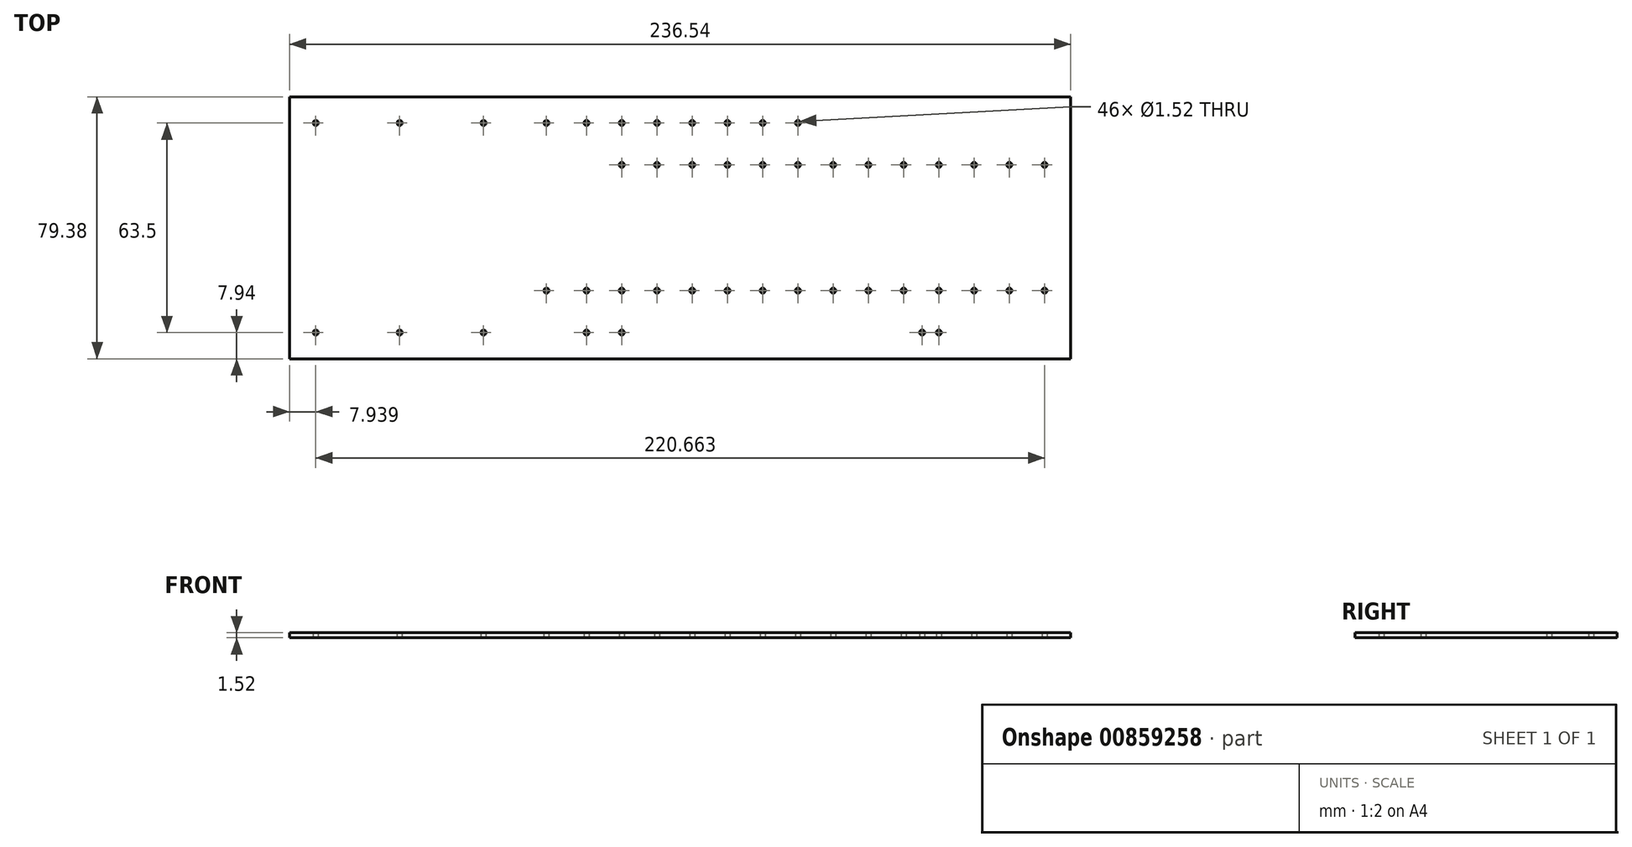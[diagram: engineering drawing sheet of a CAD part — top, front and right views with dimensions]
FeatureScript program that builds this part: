
annotation { "Feature Type Name" : "Feature", "Feature Type Description" : "" }
export const myFeature = defineFeature(function(context is Context, id is Id, definition is map)
    precondition{}
    {
        {
            var Q0;
            Q0=qCreatedBy(makeId("Top.planeOp"),FACE);
            var sketch = newSketch(context, id + "F0", { "sketchPlane" : qUnion([Q0])});
            skLineSegment(sketch, "E0.bottom", {"start": v(118.27, 39.69) * mm, "end": v(-118.27, 39.69) * mm});
            skLineSegment(sketch, "E0.top", {"start": v(118.27, -39.69) * mm, "end": v(-118.27, -39.69) * mm});
            skLineSegment(sketch, "E0.left", {"start": v(118.27, 39.69) * mm, "end": v(118.27, -39.69) * mm});
            skLineSegment(sketch, "E0.right", {"start": v(-118.27, 39.69) * mm, "end": v(-118.27, -39.69) * mm});
            skPoint(sketch, "E0.middle", {"position": v(0, 0) * mm});
            skPoint(sketch, "E1", {"position": v(-110.33, -31.75) * mm});
            skPoint(sketch, "E2", {"position": v(-84.93, -31.75) * mm});
            skPoint(sketch, "E3", {"position": v(-59.53, -31.75) * mm});
            skPoint(sketch, "E4", {"position": v(-59.53, 31.75) * mm});
            skPoint(sketch, "E5", {"position": v(-84.93, 31.75) * mm});
            skPoint(sketch, "E6", {"position": v(-110.33, 31.75) * mm});
            skPoint(sketch, "E7", {"position": v(-40.48, 31.75) * mm});
            skPoint(sketch, "E8", {"position": v(-17.68, 31.75) * mm});
            skPoint(sketch, "E9", {"position": v(-7.02, 31.75) * mm});
            skPoint(sketch, "E10", {"position": v(3.65, 31.75) * mm});
            skPoint(sketch, "E11", {"position": v(14.32, 31.75) * mm});
            skPoint(sketch, "E12", {"position": v(24.99, 31.75) * mm});
            skPoint(sketch, "E13", {"position": v(35.66, 31.75) * mm});
            skPoint(sketch, "E14", {"position": v(35.66, 19.05) * mm});
            skPoint(sketch, "E15", {"position": v(24.99, 19.05) * mm});
            skPoint(sketch, "E16", {"position": v(14.32, 19.05) * mm});
            skPoint(sketch, "E17", {"position": v(3.65, 19.05) * mm});
            skPoint(sketch, "E18", {"position": v(-7.02, 19.05) * mm});
            skPoint(sketch, "E19", {"position": v(-17.68, 19.05) * mm});
            skPoint(sketch, "E20", {"position": v(46.32, 19.05) * mm});
            skPoint(sketch, "E21", {"position": v(57, 19.05) * mm});
            skPoint(sketch, "E22", {"position": v(67.66, 19.05) * mm});
            skPoint(sketch, "E23", {"position": v(78.33, 19.05) * mm});
            skPoint(sketch, "E24", {"position": v(89, 19.05) * mm});
            skPoint(sketch, "E25", {"position": v(99.66, 19.05) * mm});
            skPoint(sketch, "E26", {"position": v(99.66, -19.05) * mm});
            skPoint(sketch, "E27", {"position": v(89, -19.05) * mm});
            skPoint(sketch, "E28", {"position": v(78.33, -19.05) * mm});
            skPoint(sketch, "E29", {"position": v(67.66, -19.05) * mm});
            skPoint(sketch, "E30", {"position": v(57, -19.05) * mm});
            skPoint(sketch, "E31", {"position": v(46.32, -19.05) * mm});
            skPoint(sketch, "E32", {"position": v(35.66, -19.05) * mm});
            skPoint(sketch, "E33", {"position": v(24.99, -19.05) * mm});
            skPoint(sketch, "E34", {"position": v(14.32, -19.05) * mm});
            skPoint(sketch, "E35", {"position": v(3.65, -19.05) * mm});
            skPoint(sketch, "E36", {"position": v(-7.02, -19.05) * mm});
            skPoint(sketch, "E37", {"position": v(-17.68, -19.05) * mm});
            skPoint(sketch, "E38", {"position": v(-40.48, -19.05) * mm});
            skPoint(sketch, "E39", {"position": v(-17.68, -31.75) * mm});
            skPoint(sketch, "E40", {"position": v(110.33, -19.05) * mm});
            skPoint(sketch, "E41", {"position": v(110.33, 19.05) * mm});
            skPoint(sketch, "E42", {"position": v(-28.35, 31.75) * mm});
            skPoint(sketch, "E43", {"position": v(-28.35, -19.05) * mm});
            skPoint(sketch, "E44", {"position": v(-28.35, -31.75) * mm});
            skCircle(sketch, "E45", {"center": v(-110.33, 31.75) * mm, "radius": 0.76 * mm});
            skCircle(sketch, "E46", {"center": v(-84.93, 31.75) * mm, "radius": 0.76 * mm});
            skCircle(sketch, "E47", {"center": v(-59.53, 31.75) * mm, "radius": 0.76 * mm});
            skCircle(sketch, "E48", {"center": v(-40.48, 31.75) * mm, "radius": 0.76 * mm});
            skCircle(sketch, "E49", {"center": v(-28.35, 31.75) * mm, "radius": 0.76 * mm});
            skCircle(sketch, "E50", {"center": v(-17.68, 31.75) * mm, "radius": 0.76 * mm});
            skCircle(sketch, "E51", {"center": v(-7.02, 31.75) * mm, "radius": 0.76 * mm});
            skCircle(sketch, "E52", {"center": v(3.65, 31.75) * mm, "radius": 0.76 * mm});
            skCircle(sketch, "E53", {"center": v(14.32, 31.75) * mm, "radius": 0.76 * mm});
            skCircle(sketch, "E54", {"center": v(24.99, 31.75) * mm, "radius": 0.76 * mm});
            skCircle(sketch, "E55", {"center": v(35.66, 31.75) * mm, "radius": 0.76 * mm});
            skCircle(sketch, "E56", {"center": v(-17.68, 19.05) * mm, "radius": 0.76 * mm});
            skCircle(sketch, "E57", {"center": v(-7.02, 19.05) * mm, "radius": 0.76 * mm});
            skCircle(sketch, "E58", {"center": v(3.65, 19.05) * mm, "radius": 0.76 * mm});
            skCircle(sketch, "E59", {"center": v(14.32, 19.05) * mm, "radius": 0.76 * mm});
            skCircle(sketch, "E60", {"center": v(24.99, 19.05) * mm, "radius": 0.76 * mm});
            skCircle(sketch, "E61", {"center": v(35.66, 19.05) * mm, "radius": 0.76 * mm});
            skCircle(sketch, "E62", {"center": v(46.32, 19.05) * mm, "radius": 0.76 * mm});
            skCircle(sketch, "E63", {"center": v(57, 19.05) * mm, "radius": 0.76 * mm});
            skCircle(sketch, "E64", {"center": v(67.66, 19.05) * mm, "radius": 0.76 * mm});
            skCircle(sketch, "E65", {"center": v(78.33, 19.05) * mm, "radius": 0.76 * mm});
            skCircle(sketch, "E66", {"center": v(89, 19.05) * mm, "radius": 0.76 * mm});
            skCircle(sketch, "E67", {"center": v(99.66, 19.05) * mm, "radius": 0.76 * mm});
            skCircle(sketch, "E68", {"center": v(110.33, 19.05) * mm, "radius": 0.76 * mm});
            skCircle(sketch, "E69", {"center": v(110.33, -19.05) * mm, "radius": 0.76 * mm});
            skCircle(sketch, "E70", {"center": v(99.66, -19.05) * mm, "radius": 0.76 * mm});
            skCircle(sketch, "E71", {"center": v(89, -19.05) * mm, "radius": 0.76 * mm});
            skCircle(sketch, "E72", {"center": v(78.33, -19.05) * mm, "radius": 0.76 * mm});
            skCircle(sketch, "E73", {"center": v(67.66, -19.05) * mm, "radius": 0.76 * mm});
            skCircle(sketch, "E74", {"center": v(57, -19.05) * mm, "radius": 0.76 * mm});
            skCircle(sketch, "E75", {"center": v(46.32, -19.05) * mm, "radius": 0.76 * mm});
            skCircle(sketch, "E76", {"center": v(35.66, -19.05) * mm, "radius": 0.76 * mm});
            skCircle(sketch, "E77", {"center": v(24.99, -19.05) * mm, "radius": 0.76 * mm});
            skCircle(sketch, "E78", {"center": v(14.32, -19.05) * mm, "radius": 0.76 * mm});
            skCircle(sketch, "E79", {"center": v(3.65, -19.05) * mm, "radius": 0.76 * mm});
            skCircle(sketch, "E80", {"center": v(-7.02, -19.05) * mm, "radius": 0.76 * mm});
            skCircle(sketch, "E81", {"center": v(-17.68, -19.05) * mm, "radius": 0.76 * mm});
            skCircle(sketch, "E82", {"center": v(-28.35, -19.05) * mm, "radius": 0.76 * mm});
            skCircle(sketch, "E83", {"center": v(-40.48, -19.05) * mm, "radius": 0.76 * mm});
            skCircle(sketch, "E84", {"center": v(-59.53, -31.75) * mm, "radius": 0.76 * mm});
            skCircle(sketch, "E85", {"center": v(-84.93, -31.75) * mm, "radius": 0.76 * mm});
            skCircle(sketch, "E86", {"center": v(-110.33, -31.75) * mm, "radius": 0.76 * mm});
            skCircle(sketch, "E87", {"center": v(-28.35, -31.75) * mm, "radius": 0.76 * mm});
            skCircle(sketch, "E88", {"center": v(-17.68, -31.75) * mm, "radius": 0.76 * mm});
            skCircle(sketch, "E89", {"center": v(78.33, -31.75) * mm, "radius": 0.76 * mm});
            skCircle(sketch, "E90", {"center": v(73.26, -31.75) * mm, "radius": 0.76 * mm});
            skSolve(sketch);
        }
        {
            var Q0;
            Q0=makeQuery(id+"F0.imprint","IMPRINT",FACE,{"disambiguationData":[TD([[makeQuery(id+"F0.imprint","IMPRINT",EDGE,{"derivedFrom":sQuery(id+"F0.wireOp",EDGE,"E0.bottom")}),1.0]])]});
            extrude(context, id + "F1", {"entities" : qUnion([Q0]), "depth" : 1.52 * mm, "offsetDistance" : 25.4 * mm});
        }
    });
